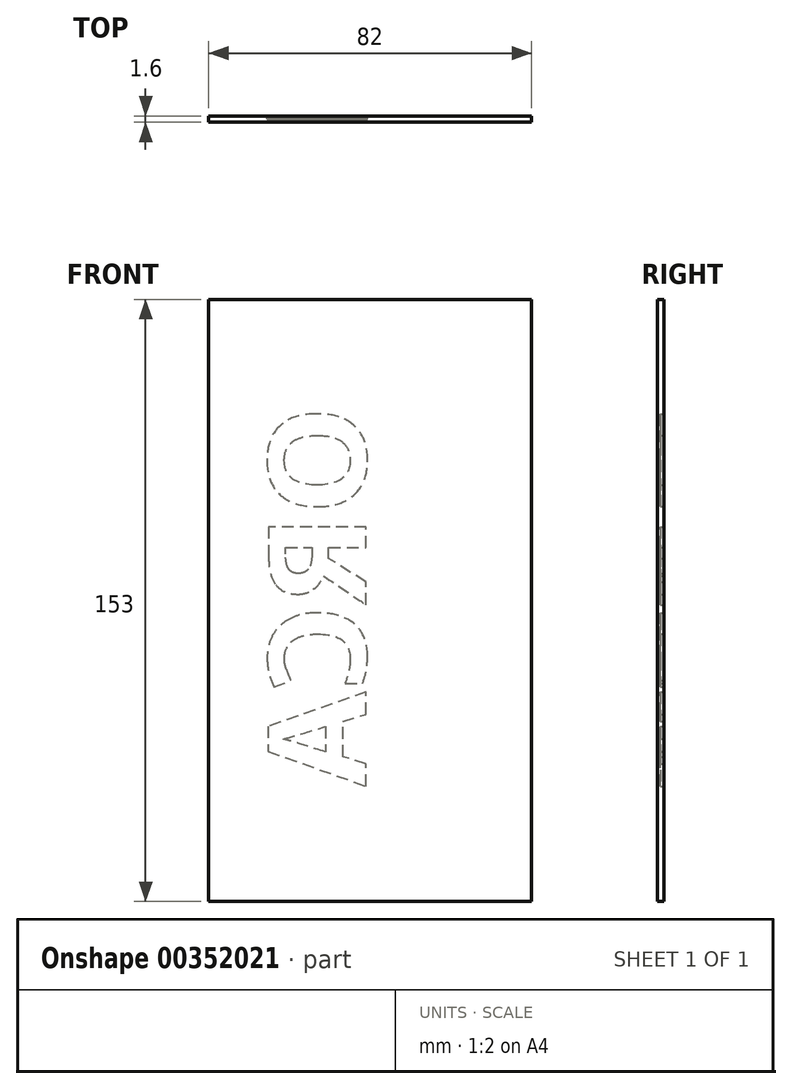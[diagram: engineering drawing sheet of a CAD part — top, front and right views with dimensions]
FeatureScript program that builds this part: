
annotation { "Feature Type Name" : "Feature", "Feature Type Description" : "" }
export const myFeature = defineFeature(function(context is Context, id is Id, definition is map)
    precondition{}
    {
        {
            var Q0;
            Q0=qCreatedBy(makeId("Front.planeOp"),FACE);
            var sketch = newSketch(context, id + "F0", { "sketchPlane" : qUnion([Q0])});
            skLineSegment(sketch, "E0", {"start": v(-82, 76.5) * mm, "end": v(0, 76.5) * mm});
            skLineSegment(sketch, "E1", {"start": v(0, 76.5) * mm, "end": v(0, -76.5) * mm});
            skLineSegment(sketch, "E2", {"start": v(0, -76.5) * mm, "end": v(-82, -76.5) * mm});
            skLineSegment(sketch, "E3", {"start": v(-82, -76.5) * mm, "end": v(-82, 76.5) * mm});
            skSolve(sketch);
        }
        {
            var Q0;
            Q0 = qSketchRegion(id + "F0", true);
            extrude(context, id + "F1", {"entities" : qUnion([Q0]), "depth" : 1.6 * mm});
        }
        {
            var Q0;
            Q0=makeQuery(id+"F1.opExtrude","CAP_FACE",FACE,{"disambiguationData":[OSD([sQuery(id+"F0.wireOp",EDGE,"E0"),sQuery(id+"F0.wireOp",EDGE,"E1"),sQuery(id+"F0.wireOp",EDGE,"E2"),sQuery(id+"F0.wireOp",EDGE,"E3")])],"isStart":true});
            var sketch = newSketch(context, id + "F2", { "sketchPlane" : qUnion([Q0])});
            skText(sketch, "E4", { "text": "ORCA", "fontName": "OpenSans-Bold.ttf"});
            const initialGuessF2  = {"E4": [0.042, 0.04945, 0, -1, 0.025]};
            skSetInitialGuess(sketch, initialGuessF2);
            skSolve(sketch);
        }
        {
            var Q0;
            Q0 = qSketchRegion(id + "F2", true);
            extrude(context, id + "F3", {"entities" : qUnion([Q0]), "operationType" : NewBodyOperationType.REMOVE, "oppositeDirection" : true, "depth" : .8 * mm});
        }
    });
